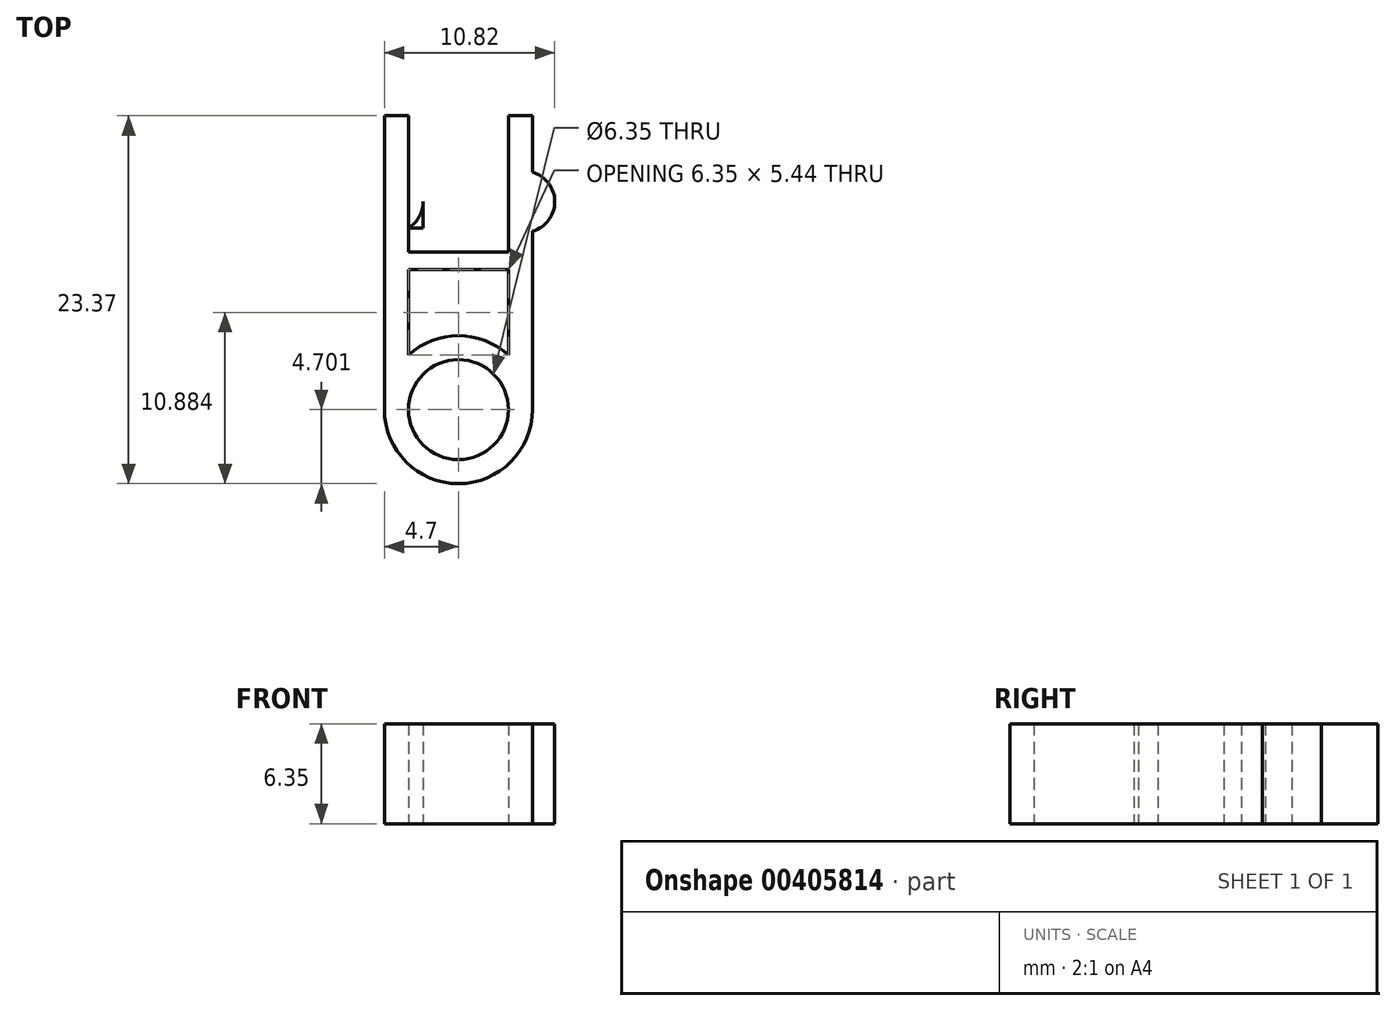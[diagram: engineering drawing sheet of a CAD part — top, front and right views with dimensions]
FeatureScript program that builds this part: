
annotation { "Feature Type Name" : "Feature", "Feature Type Description" : "" }
export const myFeature = defineFeature(function(context is Context, id is Id, definition is map)
    precondition{}
    {
        {
            var Q0;
            Q0=qCreatedBy(makeId("Top.planeOp"),FACE);
            var sketch = newSketch(context, id + "F0", { "sketchPlane" : qUnion([Q0])});
            skLineSegment(sketch, "E0", {"start": v(0, 8.65) * mm, "end": v(0, -8.65) * mm});
            skLineSegment(sketch, "E1.bottom", {"start": v(-3.17, 8.65) * mm, "end": v(3.18, 8.65) * mm});
            skLineSegment(sketch, "E1.top", {"start": v(-3.17, -8.65) * mm, "end": v(3.18, -8.65) * mm});
            skLineSegment(sketch, "E1.left", {"start": v(-3.18, 8.65) * mm, "end": v(-3.18, -8.65) * mm});
            skLineSegment(sketch, "E1.right", {"start": v(3.18, 8.65) * mm, "end": v(3.18, -8.65) * mm});
            skPoint(sketch, "E1.middle", {"position": v(0, 0) * mm});
            skLineSegment(sketch, "E2", {"start": v(-3.18, -7.12) * mm, "end": v(3.18, -7.12) * mm});
            skLineSegment(sketch, "E3", {"start": v(-3.18, -3.8) * mm, "end": v(3.18, -3.8) * mm});
            skLineSegment(sketch, "E4.bottom", {"start": v(-2.24, 8.65) * mm, "end": v(2.24, 8.65) * mm});
            skLineSegment(sketch, "E4.top", {"start": v(-2.24, -8.65) * mm, "end": v(2.24, -8.65) * mm});
            skLineSegment(sketch, "E4.left", {"start": v(-2.24, 8.65) * mm, "end": v(-2.24, -8.65) * mm});
            skLineSegment(sketch, "E4.right", {"start": v(2.24, 8.65) * mm, "end": v(2.24, -8.65) * mm});
            skCircle(sketch, "E5", {"center": v(4.18, -5.46) * mm, "radius": 1.94 * mm});
            skPoint(sketch, "E5.third.point", {"position": v(2.24, -5.46) * mm});
            skLineSegment(sketch, "E6.MirrorCS", {"start": v(3.17, -8.65) * mm, "end": v(-3.18, -8.65) * mm});
            skLineSegment(sketch, "E7.MirrorCS", {"start": v(3.17, 8.65) * mm, "end": v(-3.18, 8.65) * mm});
            skPoint(sketch, "E8.MirrorP", {"position": v(-2.24, -5.46) * mm});
            skLineSegment(sketch, "E9.MirrorCS", {"start": v(2.24, -8.65) * mm, "end": v(-2.24, -8.65) * mm});
            skLineSegment(sketch, "E10.MirrorCS", {"start": v(2.24, 8.65) * mm, "end": v(-2.24, 8.65) * mm});
            skLineSegment(sketch, "E11.MirrorCS", {"start": v(3.18, -7.12) * mm, "end": v(-3.18, -7.12) * mm});
            skLineSegment(sketch, "E12.MirrorCS", {"start": v(3.18, -3.8) * mm, "end": v(-3.18, -3.8) * mm});
            skCircle(sketch, "E13.MirrorC", {"center": v(-4.18, -5.46) * mm, "radius": 1.94 * mm});
            skLineSegment(sketch, "E14.MirrorCS", {"start": v(-3.18, 3.8) * mm, "end": v(3.18, 3.8) * mm});
            skLineSegment(sketch, "E15.MirrorCS", {"start": v(3.18, 7.12) * mm, "end": v(-3.18, 7.12) * mm});
            skLineSegment(sketch, "E16.MirrorCS", {"start": v(3.18, 3.8) * mm, "end": v(-3.18, 3.8) * mm});
            skLineSegment(sketch, "E17.MirrorCS", {"start": v(2.24, -8.65) * mm, "end": v(2.24, 8.65) * mm});
            skLineSegment(sketch, "E18.MirrorCS", {"start": v(-2.24, -8.65) * mm, "end": v(-2.24, 8.65) * mm});
            skLineSegment(sketch, "E19.MirrorCS", {"start": v(-3.18, 7.12) * mm, "end": v(3.17, 7.12) * mm});
            skLineSegment(sketch, "E20.MirrorCS", {"start": v(3.18, -8.65) * mm, "end": v(3.17, 8.65) * mm});
            skLineSegment(sketch, "E21.MirrorCS", {"start": v(0, -8.65) * mm, "end": v(0, 8.65) * mm});
            skLineSegment(sketch, "E22.MirrorCS", {"start": v(-3.18, -8.65) * mm, "end": v(-3.18, 8.65) * mm});
            skCircle(sketch, "E23.MirrorC", {"center": v(-4.18, 5.46) * mm, "radius": 1.94 * mm});
            skCircle(sketch, "E24.MirrorC", {"center": v(4.18, 5.46) * mm, "radius": 1.94 * mm});
            skLineSegment(sketch, "E25.MirrorCS", {"start": v(-3.17, -8.65) * mm, "end": v(-3.17, 8.65) * mm});
            skPoint(sketch, "E26.MirrorP", {"position": v(-2.24, 5.46) * mm});
            skLineSegment(sketch, "E27.MirrorCS", {"start": v(3.18, -8.65) * mm, "end": v(3.18, 8.65) * mm});
            skPoint(sketch, "E28.MirrorP", {"position": v(2.24, 5.46) * mm});
            skLineSegment(sketch, "E29.bottom", {"start": v(-4.7, 0) * mm, "end": v(4.7, 0) * mm});
            skLineSegment(sketch, "E29.top", {"start": v(-4.7, -23.37) * mm, "end": v(4.7, -23.37) * mm});
            skLineSegment(sketch, "E29.left", {"start": v(-4.7, 0) * mm, "end": v(-4.7, -23.37) * mm});
            skLineSegment(sketch, "E29.right", {"start": v(4.7, 0) * mm, "end": v(4.7, -23.37) * mm});
            skCircle(sketch, "E30", {"center": v(0, -18.67) * mm, "radius": 3.18 * mm});
            skCircle(sketch, "E31", {"center": v(0, -18.67) * mm, "radius": 4.7 * mm});
            skLineSegment(sketch, "E32", {"start": v(-4.7, -9.77) * mm, "end": v(4.7, -9.77) * mm});
            skLineSegment(sketch, "E33", {"start": v(3.18, -8.65) * mm, "end": v(3.18, -18.67) * mm});
            skLineSegment(sketch, "E34", {"start": v(-3.17, -8.65) * mm, "end": v(-3.17, -18.67) * mm});
            skSolve(sketch);
        }
        {
            var Q0;
            {var subQ5=sQuery(id+"F0.wireOp",EDGE,"E30");var subQ8=sQuery(id+"F0.wireOp",EDGE,"E33");var subQ10=makeQuery(id+"F0.imprint","INTERSECT",VERTEX,{"derivedFrom":[subQ5,subQ8]});Q0=makeQuery(id+"F0.imprint","IMPRINT",FACE,{"disambiguationData":[TD([[makeQuery(id+"F0.imprint","IMPRINT",EDGE,{"disambiguationData":[TD([[subQ10,1.0]])],"derivedFrom":subQ5}),-1.0]])]});}
            var Q1;
            {var subQ0=sQuery(id+"F0.wireOp",EDGE,"E32");var subQ1=sQuery(id+"F0.wireOp",EDGE,"E29.left");var subQ2=makeQuery(id+"F0.imprint","INTERSECT",VERTEX,{"derivedFrom":[subQ1,subQ0]});Q1=makeQuery(id+"F0.imprint","IMPRINT",FACE,{"disambiguationData":[TD([[makeQuery(id+"F0.imprint","IMPRINT",EDGE,{"disambiguationData":[TD([[subQ2,-1.0]])],"derivedFrom":subQ1}),1.0]])]});}
            var Q2;
            {var subQ0=sQuery(id+"F0.wireOp",EDGE,"E32");var subQ1=sQuery(id+"F0.wireOp",EDGE,"E29.right");var subQ2=makeQuery(id+"F0.imprint","INTERSECT",VERTEX,{"derivedFrom":[subQ1,subQ0]});Q2=makeQuery(id+"F0.imprint","IMPRINT",FACE,{"disambiguationData":[TD([[makeQuery(id+"F0.imprint","IMPRINT",EDGE,{"disambiguationData":[TD([[subQ2,-1.0]])],"derivedFrom":subQ1}),-1.0]])]});}
            var Q3;
            {var subQ0=sQuery(id+"F0.wireOp",EDGE,"E33");var subQ1=sQuery(id+"F0.wireOp",EDGE,"E30");var subQ2=makeQuery(id+"F0.imprint","INTERSECT",VERTEX,{"derivedFrom":[subQ1,subQ0]});Q3=makeQuery(id+"F0.imprint","IMPRINT",FACE,{"disambiguationData":[TD([[makeQuery(id+"F0.imprint","IMPRINT",EDGE,{"disambiguationData":[TD([[subQ2,-1.0]])],"derivedFrom":subQ1}),-1.0]])]});}
            var Q4;
            {var subQ7=sQuery(id+"F0.wireOp",EDGE,"E34");var subQ9=sQuery(id+"F0.wireOp",EDGE,"E32");var subQ10=makeQuery(id+"F0.imprint","INTERSECT",VERTEX,{"derivedFrom":[subQ9,subQ7]});Q4=makeQuery(id+"F0.imprint","IMPRINT",FACE,{"disambiguationData":[TD([[makeQuery(id+"F0.imprint","IMPRINT",EDGE,{"disambiguationData":[TD([[subQ10,-1.0]])],"derivedFrom":subQ9}),1.0]])]});}
            var Q5;
            {var subQ0=sQuery(id+"F0.wireOp",EDGE,"E32");var subQ1=sQuery(id+"F0.wireOp",EDGE,"E29.right");var subQ2=makeQuery(id+"F0.imprint","INTERSECT",VERTEX,{"derivedFrom":[subQ1,subQ0]});Q5=makeQuery(id+"F0.imprint","IMPRINT",FACE,{"disambiguationData":[TD([[makeQuery(id+"F0.imprint","IMPRINT",EDGE,{"disambiguationData":[TD([[subQ2,1.0]])],"derivedFrom":subQ1}),-1.0]])]});}
            var Q6;
            {var subQ0=sQuery(id+"F0.wireOp",EDGE,"E32");var subQ1=sQuery(id+"F0.wireOp",EDGE,"E29.left");var subQ2=makeQuery(id+"F0.imprint","INTERSECT",VERTEX,{"derivedFrom":[subQ1,subQ0]});Q6=makeQuery(id+"F0.imprint","IMPRINT",FACE,{"disambiguationData":[TD([[makeQuery(id+"F0.imprint","IMPRINT",EDGE,{"disambiguationData":[TD([[subQ2,1.0]])],"derivedFrom":subQ1}),1.0]])]});}
            var Q7;
            {var subQ0=sQuery(id+"F0.wireOp",EDGE,"E13.MirrorC");var subQ4=sQuery(id+"F0.wireOp",EDGE,"E29.left");var subQ5=makeQuery(id+"F0.imprint","INTERSECT",VERTEX,{"disambiguationData":[OD(0.0)],"derivedFrom":[subQ0,subQ4]});Q7=makeQuery(id+"F0.imprint","IMPRINT",FACE,{"disambiguationData":[TD([[makeQuery(id+"F0.imprint","IMPRINT",EDGE,{"disambiguationData":[TD([[subQ5,-1.0]])],"derivedFrom":subQ4}),1.0]])]});}
            var Q8;
            {var subQ0=sQuery(id+"F0.wireOp",EDGE,"E13.MirrorC");var subQ4=makeQuery(id+"F0.imprint","INTERSECT",VERTEX,{"derivedFrom":[sQuery(id+"F0.wireOp",EDGE,"E4.left"),subQ0]});Q8=makeQuery(id+"F0.imprint","IMPRINT",FACE,{"disambiguationData":[TD([[makeQuery(id+"F0.imprint","IMPRINT",EDGE,{"disambiguationData":[TD([[subQ4,1.0]])],"derivedFrom":subQ0}),-1.0]])]});}
            var Q9;
            {var subQ1=sQuery(id+"F0.wireOp",EDGE,"E5");var subQ3=makeQuery(id+"F0.imprint","INTERSECT",VERTEX,{"derivedFrom":[subQ1,sQuery(id+"F0.wireOp",EDGE,"E17.MirrorCS")]});Q9=makeQuery(id+"F0.imprint","IMPRINT",FACE,{"disambiguationData":[TD([[makeQuery(id+"F0.imprint","IMPRINT",EDGE,{"disambiguationData":[TD([[subQ3,1.0]])],"derivedFrom":subQ1}),1.0]])]});}
            var Q10;
            {var subQ1=sQuery(id+"F0.wireOp",EDGE,"E5");var subQ3=sQuery(id+"F0.wireOp",EDGE,"E29.right");var subQ4=makeQuery(id+"F0.imprint","INTERSECT",VERTEX,{"disambiguationData":[OD(0.0)],"derivedFrom":[subQ1,subQ3]});Q10=makeQuery(id+"F0.imprint","IMPRINT",FACE,{"disambiguationData":[TD([[makeQuery(id+"F0.imprint","IMPRINT",EDGE,{"disambiguationData":[TD([[subQ4,-1.0]])],"derivedFrom":subQ3}),-1.0]])]});}
            var Q11;
            {var subQ3=sQuery(id+"F0.wireOp",EDGE,"E29.right");var subQ5=sQuery(id+"F0.wireOp",EDGE,"E29.bottom");var subQ7=makeQuery(id+"F0.imprint","INTERSECT",VERTEX,{"derivedFrom":[subQ5,subQ3]});Q11=makeQuery(id+"F0.imprint","IMPRINT",FACE,{"disambiguationData":[TD([[makeQuery(id+"F0.imprint","IMPRINT",EDGE,{"disambiguationData":[TD([[subQ7,1.0]])],"derivedFrom":subQ5}),-1.0]])]});}
            var Q12;
            {var subQ3=sQuery(id+"F0.wireOp",EDGE,"E29.bottom");var subQ5=sQuery(id+"F0.wireOp",EDGE,"E29.left");var subQ7=makeQuery(id+"F0.imprint","INTERSECT",VERTEX,{"derivedFrom":[subQ3,subQ5]});Q12=makeQuery(id+"F0.imprint","IMPRINT",FACE,{"disambiguationData":[TD([[makeQuery(id+"F0.imprint","IMPRINT",EDGE,{"disambiguationData":[TD([[subQ7,-1.0]])],"derivedFrom":subQ3}),-1.0]])]});}
            extrude(context, id + "F1", {"entities" : qUnion([Q0, Q1, Q2, Q3, Q4, Q5, Q6, Q7, Q8, Q9, Q10, Q11, Q12]), "depth" : 6.35 * mm});
        }
    });
